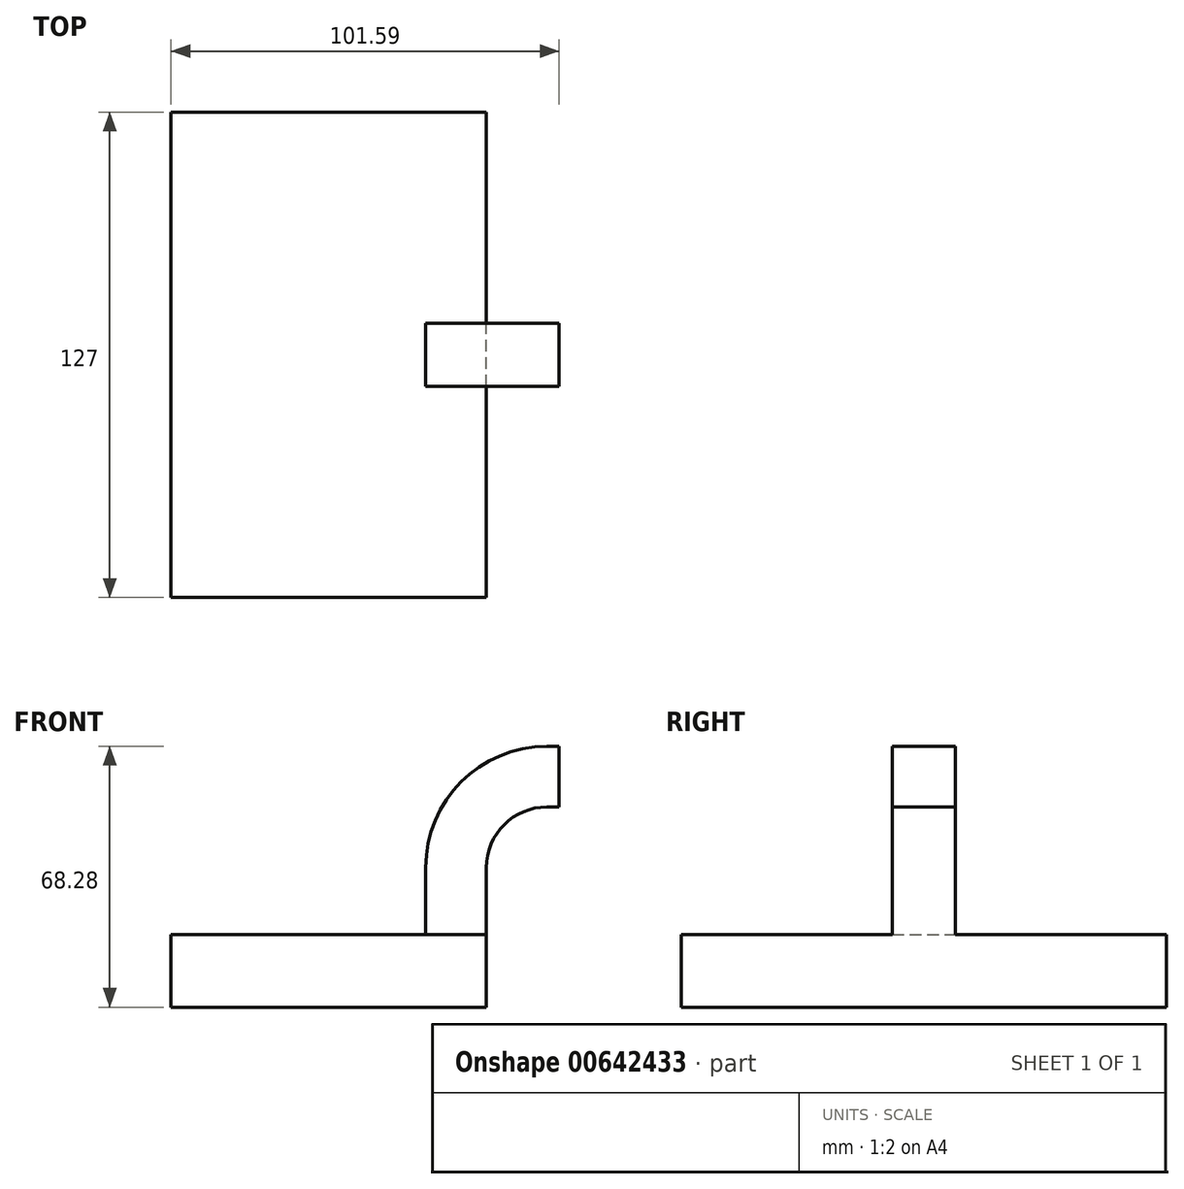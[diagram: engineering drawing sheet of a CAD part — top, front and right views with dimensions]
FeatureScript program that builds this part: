
annotation { "Feature Type Name" : "Feature", "Feature Type Description" : "" }
export const myFeature = defineFeature(function(context is Context, id is Id, definition is map)
    precondition{}
    {
        {
            var Q0;
            Q0=qCreatedBy(makeId("Front.planeOp"),FACE);
            var sketch = newSketch(context, id + "F0", { "sketchPlane" : qUnion([Q0])});
            skLineSegment(sketch, "E0.bottom", {"start": v(-41.28, 9.52) * mm, "end": v(41.28, 9.52) * mm});
            skLineSegment(sketch, "E0.top", {"start": v(-41.28, -9.53) * mm, "end": v(41.28, -9.53) * mm});
            skLineSegment(sketch, "E0.left", {"start": v(-41.28, 9.52) * mm, "end": v(-41.28, -9.53) * mm});
            skLineSegment(sketch, "E0.right", {"start": v(41.28, 9.52) * mm, "end": v(41.28, -9.53) * mm});
            skPoint(sketch, "E0.middle", {"position": v(0, 0) * mm});
            skLineSegment(sketch, "E1.bottom", {"start": v(60.33, 66.67) * mm, "end": v(111.13, 66.67) * mm});
            skLineSegment(sketch, "E1.top", {"start": v(60.33, 38.1) * mm, "end": v(111.13, 38.1) * mm});
            skLineSegment(sketch, "E1.left", {"start": v(60.32, 66.67) * mm, "end": v(60.32, 38.1) * mm});
            skLineSegment(sketch, "E1.right", {"start": v(111.12, 66.67) * mm, "end": v(111.12, 38.1) * mm});
            skPoint(sketch, "E1.middle", {"position": v(85.73, 52.39) * mm});
            skLineSegment(sketch, "E2", {"start": v(41.28, 9.52) * mm, "end": v(41.28, 27) * mm});
            skArc(sketch, "E3", {"start": v(41.28, 27) * mm, "mid": v(45.92, 38.22) * mm, "end": v(57.15, 42.87) * mm});
            skLineSegment(sketch, "E4", {"start": v(57.15, 42.87) * mm, "end": v(91.9, 42.87) * mm});
            skLineSegment(sketch, "E5.0", {"start": v(57.15, 58.75) * mm, "end": v(92.4, 58.75) * mm});
            skArc(sketch, "E5.1", {"start": v(25.4, 27) * mm, "mid": v(34.7, 49.45) * mm, "end": v(57.15, 58.75) * mm});
            skLineSegment(sketch, "E5.2", {"start": v(25.4, 11.79) * mm, "end": v(25.4, 27) * mm});
            skLineSegment(sketch, "E5.3", {"start": v(25.4, 11.79) * mm, "end": v(25.4, -7.26) * mm});
            skLineSegment(sketch, "E6", {"start": v(92.28, 38.1) * mm, "end": v(92.4, 66.67) * mm});
            skFitSpline(sketch, "E7", {"points": [v(-41.28, 9.52) * mm, v(57.15, 58.75) * mm], "startDerivative": vector(20.75, 118.7) * mm, "endDerivative": vector(140.44, -9.6) * mm});
            skSolve(sketch);
        }
        {
            var Q0;
            Q0=makeQuery(id+"F0.imprint","IMPRINT",FACE,{"disambiguationData":[TD([[makeQuery(id+"F0.imprint","IMPRINT",EDGE,{"derivedFrom":sQuery(id+"F0.wireOp",EDGE,"E0.top")}),1.0]])]});
            extrude(context, id + "F1", {"entities" : qUnion([Q0]), "endBound" : BoundingType.SYMMETRIC, "depth" : 127 * mm, "offsetDistance" : 25.4 * mm});
        }
        {
            var Q0;
            Q0=makeQuery(id+"F0.imprint","IMPRINT",FACE,{"disambiguationData":[TD([[makeQuery(id+"F0.imprint","IMPRINT",EDGE,{"derivedFrom":sQuery(id+"F0.wireOp",EDGE,"E5.1")}),1.0]])]});
            extrude(context, id + "F2", {"entities" : qUnion([Q0]), "operationType" : NewBodyOperationType.ADD, "endBound" : BoundingType.SYMMETRIC, "depth" : 16.5 * mm, "offsetDistance" : 25.4 * mm});
        }
    });
